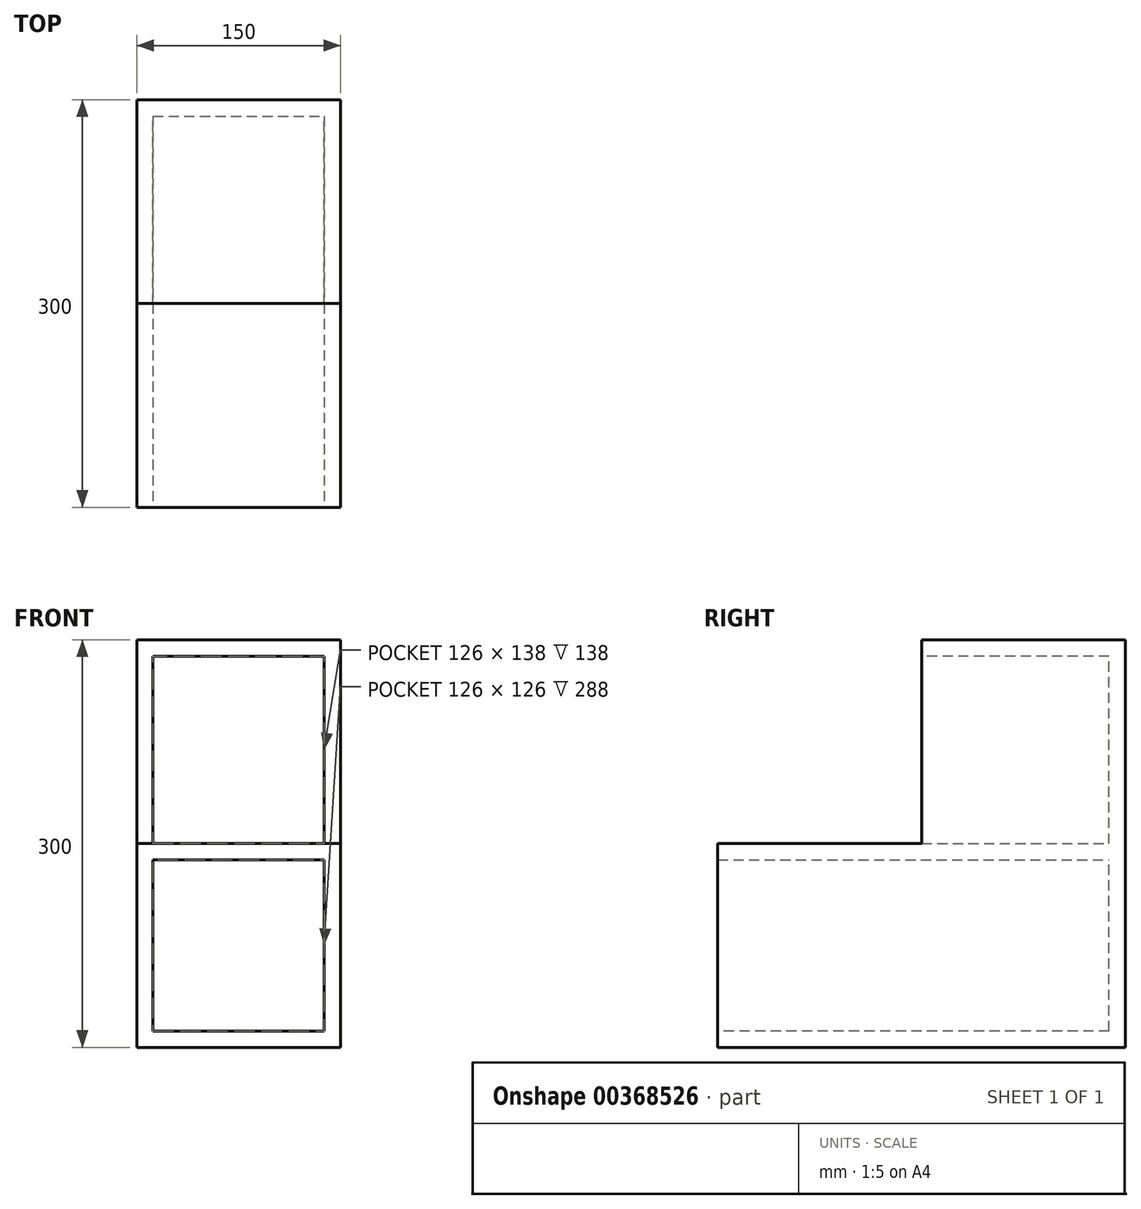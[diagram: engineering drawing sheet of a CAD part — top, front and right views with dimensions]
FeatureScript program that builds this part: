
annotation { "Feature Type Name" : "Feature", "Feature Type Description" : "" }
export const myFeature = defineFeature(function(context is Context, id is Id, definition is map)
    precondition{}
    {
        {
            var Q0;
            Q0=qCreatedBy(makeId("Right.planeOp"),FACE);
            var sketch = newSketch(context, id + "F0", { "sketchPlane" : qUnion([Q0])});
            skLineSegment(sketch, "E0.bottom", {"start": v(150, -150) * mm, "end": v(-150, -150) * mm});
            skLineSegment(sketch, "E0.top", {"start": v(150, 150) * mm, "end": v(-150, 150) * mm});
            skLineSegment(sketch, "E0.left", {"start": v(150, -150) * mm, "end": v(150, 150) * mm});
            skLineSegment(sketch, "E0.right", {"start": v(-150, -150) * mm, "end": v(-150, 150) * mm});
            skPoint(sketch, "E0.middle", {"position": v(0, 0) * mm});
            skLineSegment(sketch, "E1.bottom", {"start": v(0, 0) * mm, "end": v(-150, 0) * mm});
            skLineSegment(sketch, "E1.top", {"start": v(0, 150) * mm, "end": v(-150, 150) * mm});
            skLineSegment(sketch, "E1.left", {"start": v(0, 0) * mm, "end": v(0, 150) * mm});
            skLineSegment(sketch, "E1.right", {"start": v(-150, 0) * mm, "end": v(-150, 150) * mm});
            skSolve(sketch);
        }
        {
            var Q0;
            Q0=makeQuery(id+"F0.imprint","IMPRINT",FACE,{"disambiguationData":[TD([[makeQuery(id+"F0.imprint","IMPRINT",EDGE,{"derivedFrom":sQuery(id+"F0.wireOp",EDGE,"E0.bottom")}),-1.0]])]});
            extrude(context, id + "F1", {"entities" : qUnion([Q0]), "depth" : 150 * mm});
        }
        {
            var Q0;
            Q0=makeQuery(id+"F1.opExtrude","SWEPT_FACE",FACE,{"disambiguationData":[OSD([sQuery(id+"F0.wireOp",EDGE,"E1.left")])]});
            var Q1;
            Q1=makeQuery(id+"F1.opExtrude","SWEPT_FACE",FACE,{"disambiguationData":[OSD([sQuery(id+"F0.wireOp",EDGE,"E1.bottom")])]});
            var Q2;
            Q2=makeQuery(id+"F1.opExtrude","SWEPT_FACE",FACE,{"disambiguationData":[OSD([sQuery(id+"F0.wireOp",EDGE,"E0.right")])]});
            shell(context, id + "F2", {"entities" : qUnion([Q0, Q1, Q2]), "thickness" : 12 * mm});
        }
        {
            var Q0;
            Q0=makeQuery(id+"F1.opExtrude","CAP_FACE",FACE,{"disambiguationData":[OSD([sQuery(id+"F0.wireOp",EDGE,"E0.bottom"),sQuery(id+"F0.wireOp",EDGE,"E0.top"),sQuery(id+"F0.wireOp",EDGE,"E0.left"),sQuery(id+"F0.wireOp",EDGE,"E0.right"),sQuery(id+"F0.wireOp",EDGE,"E1.bottom"),sQuery(id+"F0.wireOp",EDGE,"E1.left")])],"isStart":false});
            var sketch = newSketch(context, id + "F3", { "sketchPlane" : qUnion([Q0])});
            skLineSegment(sketch, "E2.bottom", {"start": v(-150, 0) * mm, "end": v(150, 0) * mm});
            skLineSegment(sketch, "E2.top", {"start": v(-150, -12) * mm, "end": v(150, -12) * mm});
            skLineSegment(sketch, "E2.left", {"start": v(-150, 0) * mm, "end": v(-150, -12) * mm});
            skLineSegment(sketch, "E2.right", {"start": v(150, 0) * mm, "end": v(150, -12) * mm});
            skSolve(sketch);
        }
        {
            var Q0;
            Q0=makeQuery(id+"F3.imprint","IMPRINT",FACE,{"disambiguationData":[TD([[makeQuery(id+"F3.imprint","IMPRINT",EDGE,{"derivedFrom":sQuery(id+"F3.wireOp",EDGE,"E2.top")}),1.0]])]});
            extrude(context, id + "F4", {"entities" : qUnion([Q0]), "operationType" : NewBodyOperationType.ADD, "oppositeDirection" : true, "depth" : 150 * mm});
        }
    });
